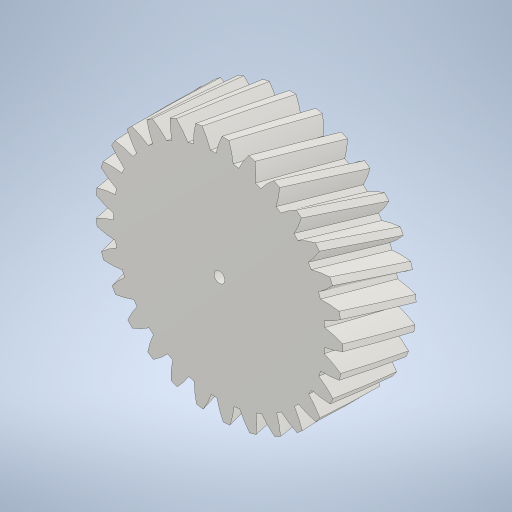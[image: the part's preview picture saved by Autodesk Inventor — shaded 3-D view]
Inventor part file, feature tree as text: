
AUTODESK INVENTOR PART (.ipt)
format: ipt  version: 2024.1 (Build 281209000, 209)  size: 583,680 bytes
history: native  units: mm (DEFAULTED — no unit token found)
features: plane x3, other x3, extrude x2, sketch x2
ambient origin geometry x8: Origin, YZ Plane, XZ Plane, XY Plane, X Axis, Y Axis, Z Axis, Center Point
bodies: Solid1 (feature_tree)
feature tree (10):
  extrude  "Extrusion1"  Depth=14.0mm TaperAngle=0.0deg
  plane  "Work Plane2"
  plane  "Work Plane8"
  plane  "Work Plane9"
  other  "Spur Gear"
  extrude  "Extrusion2"  Depth=10.0mm TaperAngle=0.0deg
  sketch  "Sketch1"  dims[d0=47.162774mm d1=14.0mm d2=0.0mm]
  other  "Srf1"
  sketch  "Sketch3"  dims[d3=45.034514mm d4=10.0mm d5=0.0mm d16=45.0mm d17=0.0mm d34=1.083308mm d39=0.0mm d41=0.0mm d43=45.0mm d46=45.0mm d47=0.0mm d48=0.0mm d49=2.09mm d50=0.0mm d51=0.0mm]
  other  "Pitch Diameter"
